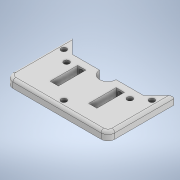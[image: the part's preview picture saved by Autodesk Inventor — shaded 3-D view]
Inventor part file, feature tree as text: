
AUTODESK INVENTOR PART (.ipt)
format: ipt  version: 2020 (Build 240168000, 168)  size: 180,736 bytes
history: native  units: in
note: dims shown in document units (in); Inventor stores cm internally (conversion verified against a paired STEP export)
features: extrude x5, sketch x5, fillet x2
ambient origin geometry x8: Origin, YZ Plane, XZ Plane, XY Plane, X Axis, Y Axis, Z Axis, Center Point
bodies: Solid1 (feature_tree)
feature tree (12):
  extrude  "Extrusion1"  Depth=2.9134in
  fillet  "Fillet1"  Radius=0.2362in
  extrude  "Extrusion2"  Depth=0.4724in
  extrude  "Extrusion3"  TaperAngle=135.0deg  [1 undecoded]
  extrude  "Extrusion4"  TaperAngle=135.0deg  [1 undecoded]
  fillet  "Fillet2"  Radius=0.1575in
  extrude  "Extrusion5"  Depth=0.3937in
  sketch  "Sketch1"  dims[d0=2.9134in d1=2.9134in d2=0.2362in d3=0.0in]
  sketch  "Sketch2"  dims[d4=0.1969in d5=0.4724in]
  sketch  "Sketch3"  dims[d6=0.7874in d7=135.0deg]
  sketch  "Sketch4"  dims[d8=0.7874in d9=135.0deg d10=0.1575in]
  sketch  "Sketch5"  dims[d11=0.1575in d12=0.1575in d13=0.3937in d14=0.0in d15=0.2362in d16=0.7874in d17=0.2362in d18=0.3937in d19=0.0in d20=0.1575in d21=0.1575in d22=0.3937in d23=0.0in d24=0.0787in d25=0.1575in d26=0.1575in d27=0.3937in d28=0.0in]
note: 2 required parameter values undecoded (feature->parameter linkage not recoverable at this tier; creation-order binding heuristic only, values carry confidence <= 0.55)
